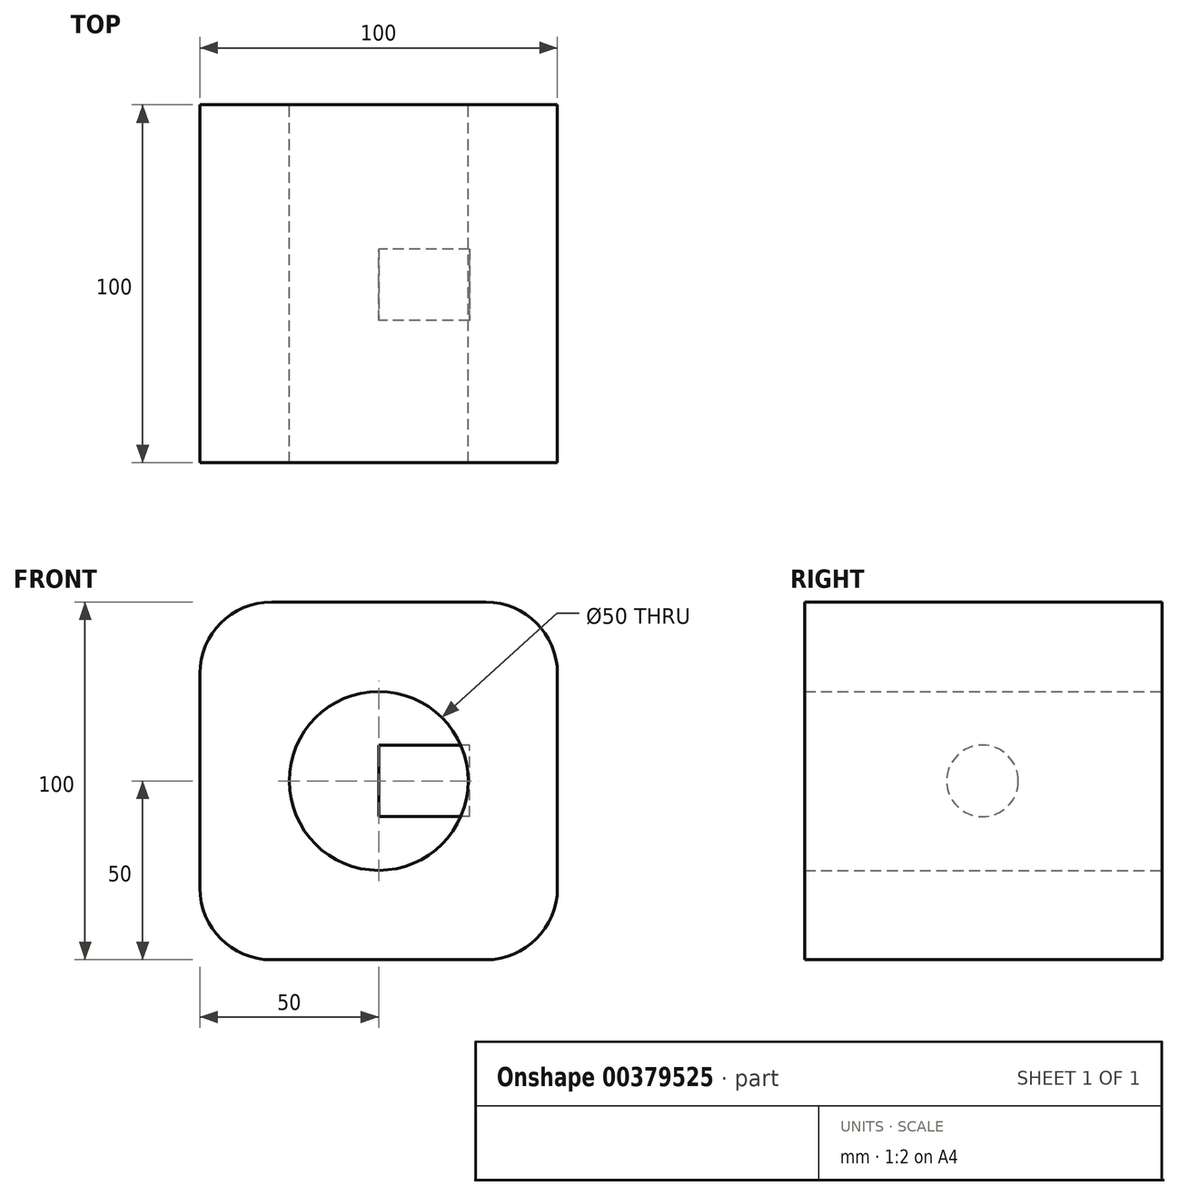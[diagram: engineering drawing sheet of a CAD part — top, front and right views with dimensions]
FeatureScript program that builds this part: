
annotation { "Feature Type Name" : "Feature", "Feature Type Description" : "" }
export const myFeature = defineFeature(function(context is Context, id is Id, definition is map)
    precondition{}
    {
        {
            var Q0;
            Q0=qCreatedBy(makeId("Front.planeOp"),FACE);
            var sketch = newSketch(context, id + "F0", { "sketchPlane" : qUnion([Q0])});
            skLineSegment(sketch, "E0.bottom", {"start": v(30, 50) * mm, "end": v(-30, 50) * mm});
            skLineSegment(sketch, "E0.top", {"start": v(30, -50) * mm, "end": v(-30, -50) * mm});
            skLineSegment(sketch, "E0.left", {"start": v(50, 30) * mm, "end": v(50, -30) * mm});
            skLineSegment(sketch, "E0.right", {"start": v(-50, 30) * mm, "end": v(-50, -30) * mm});
            skPoint(sketch, "E0.middle", {"position": v(0, 0) * mm});
            skPoint(sketch, "E1.visualSharp", {"position": v(-50, 50) * mm});
            skArc(sketch, "E1.filletArc", {"start": v(-30, 50) * mm, "mid": v(-44.14, 44.14) * mm, "end": v(-50, 30) * mm});
            skPoint(sketch, "E2.visualSharp", {"position": v(50, 50) * mm});
            skArc(sketch, "E2.filletArc", {"start": v(50, 30) * mm, "mid": v(44.14, 44.14) * mm, "end": v(30, 50) * mm});
            skPoint(sketch, "E3.visualSharp", {"position": v(50, -50) * mm});
            skArc(sketch, "E3.filletArc", {"start": v(30, -50) * mm, "mid": v(44.14, -44.14) * mm, "end": v(50, -30) * mm});
            skPoint(sketch, "E4.visualSharp", {"position": v(-50, -50) * mm});
            skArc(sketch, "E4.filletArc", {"start": v(-50, -30) * mm, "mid": v(-44.14, -44.14) * mm, "end": v(-30, -50) * mm});
            skCircle(sketch, "E5", {"center": v(0, 0) * mm, "radius": 25 * mm});
            skSolve(sketch);
        }
        {
            var Q0;
            Q0 = qSketchRegion(id + "F0", true);
            extrude(context, id + "F1", {"entities" : qUnion([Q0]), "depth" : 100 * mm});
        }
        {
            var Q0;
            Q0=qCreatedBy(makeId("Right.planeOp"),FACE);
            var sketch = newSketch(context, id + "F2", { "sketchPlane" : qUnion([Q0])});
            skCircle(sketch, "E6", {"center": v(-50.29, 0) * mm, "radius": 10 * mm});
            skSolve(sketch);
        }
        {
            var Q0;
            Q0 = qSketchRegion(id + "F2", true);
            extrude(context, id + "F3", {"entities" : qUnion([Q0]), "depth" : 25.4 * mm});
        }
    });
